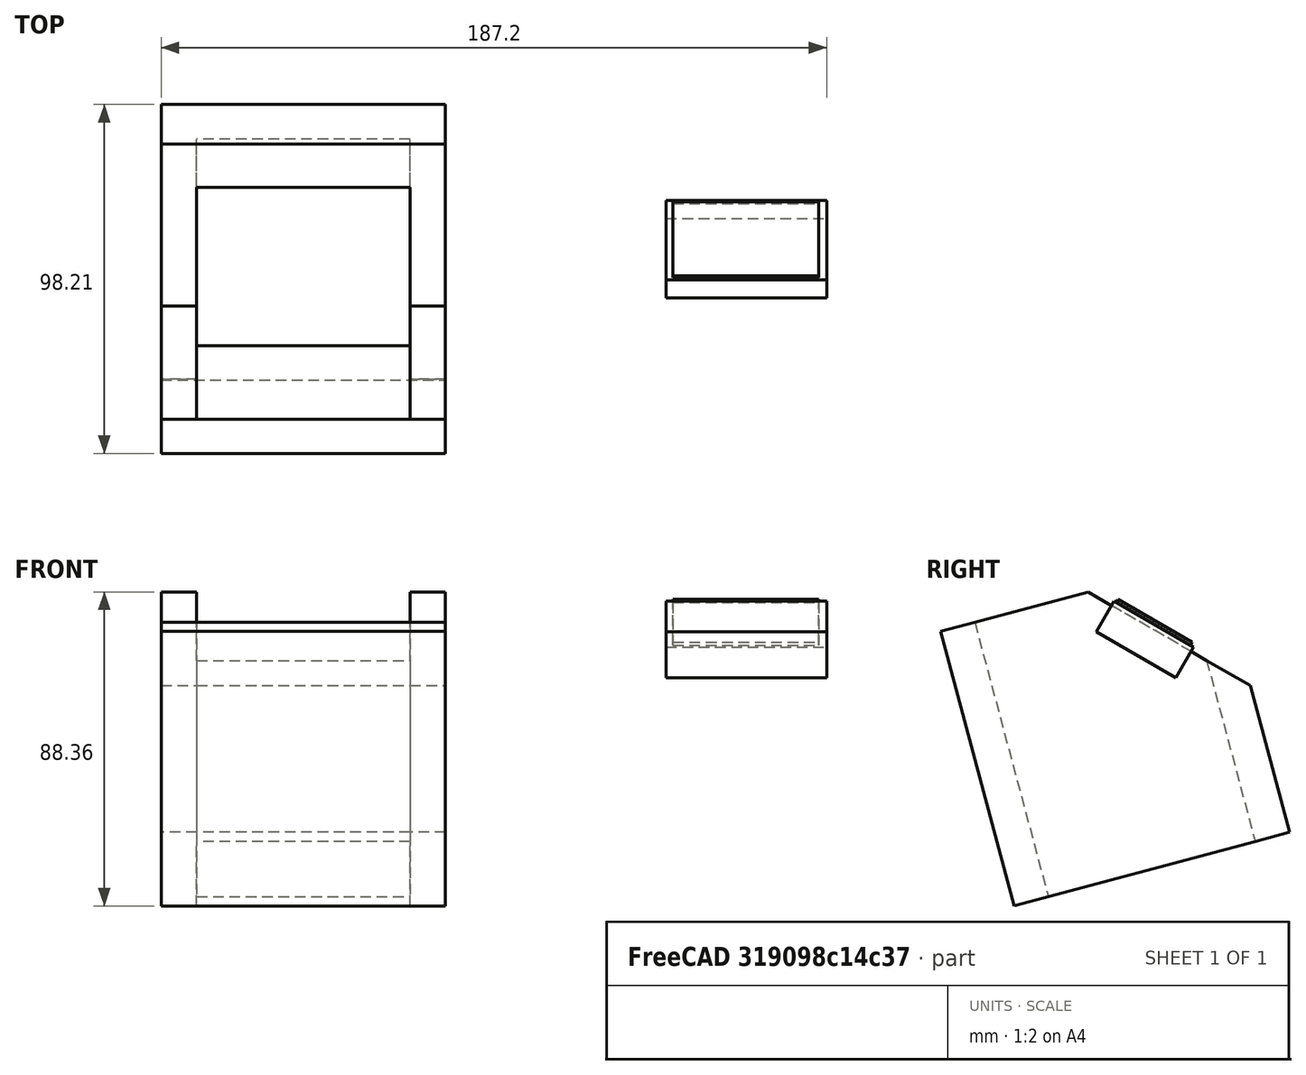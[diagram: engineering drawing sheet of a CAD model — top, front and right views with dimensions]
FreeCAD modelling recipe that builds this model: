
FCSTD DOCUMENT  (FreeCAD 0.17R13541 (Git))
Label: Power Supply Case
License: All rights reserved
LicenseURL: http://en.wikipedia.org/wiki/All_rights_reserved
objects: Part::Box×7, Part::MultiFuse×2, Part::Fuse×1, Part::Cut×1
note: 11 computed .brp shape members not serialized (recipe doc carries the construction recipe); baked Part::Feature solids carry a one-line shape summary decoded from their .brp

FEATURE [Part::Box] Box  label="Cube"
  AttacherType = Attacher::AttachEngine3D
  Height = 25.8
  Length = 45.2
  Width = 10
FEATURE [Part::Box] Box001  label="Cube001"
  AttacherType = Attacher::AttachEngine3D
  Height = 24
  Length = 41
  Placement = pos=(2,1,1) rot=(0,0,1;0rad)
  Width = 10
FEATURE [Part::Fuse] Fusion  label="Volt/Amp Meter"
  Base = -> Box
  Placement = pos=(129,-12.0766,6.23713) rot=(1,0,0;1.0472rad)
  Tool = -> Box001
FEATURE [Part::Box] Box002  label="Cube002"
  AttacherType = Attacher::AttachEngine3D
  Height = 80
  Length = 10
  Placement = pos=(67,10.3001,-39.8541) rot=(0.129428,-0.129428,0.983106;1.58783rad)
  Width = 80
FEATURE [Part::Box] Box003  label="Cube003"
  AttacherType = Attacher::AttachEngine3D
  Height = 80
  Length = 10
  Placement = pos=(57,-57.3147,-57.9714) rot=(1,0,0;0.261799rad)
  Width = 80
FEATURE [Part::Box] Box004  label="Cube004"
  AttacherType = Attacher::AttachEngine3D
  Height = 80
  Length = 10
  Placement = pos=(-13,-57.3147,-57.9714) rot=(1,0,0;0.261799rad)
  Width = 80
FEATURE [Part::MultiFuse] Fusion001
  Shapes = -> [Box002,Box004,Box003]
FEATURE [Part::Box] Box006  label="Cube006"
  AttacherType = Attacher::AttachEngine3D
  Height = 82
  Length = 40
  Placement = pos=(-14,20.0282,-2.39435) rot=(0.694747,0.186157,0.694747;2.77349rad)
  Width = 80
FEATURE [Part::Cut] Cut
  Base = -> Fusion001
  Tool = -> Box006
FEATURE [Part::Box] Box007  label="Cube007"
  AttacherType = Attacher::AttachEngine3D
  Height = 80
  Length = 80
  Placement = pos=(-13,-57.5451,-57.9877) rot=(1,0,0;0.261799rad)
  Width = 10
FEATURE [Part::MultiFuse] Fusion002
  Shapes = -> [Box007,Cut]
